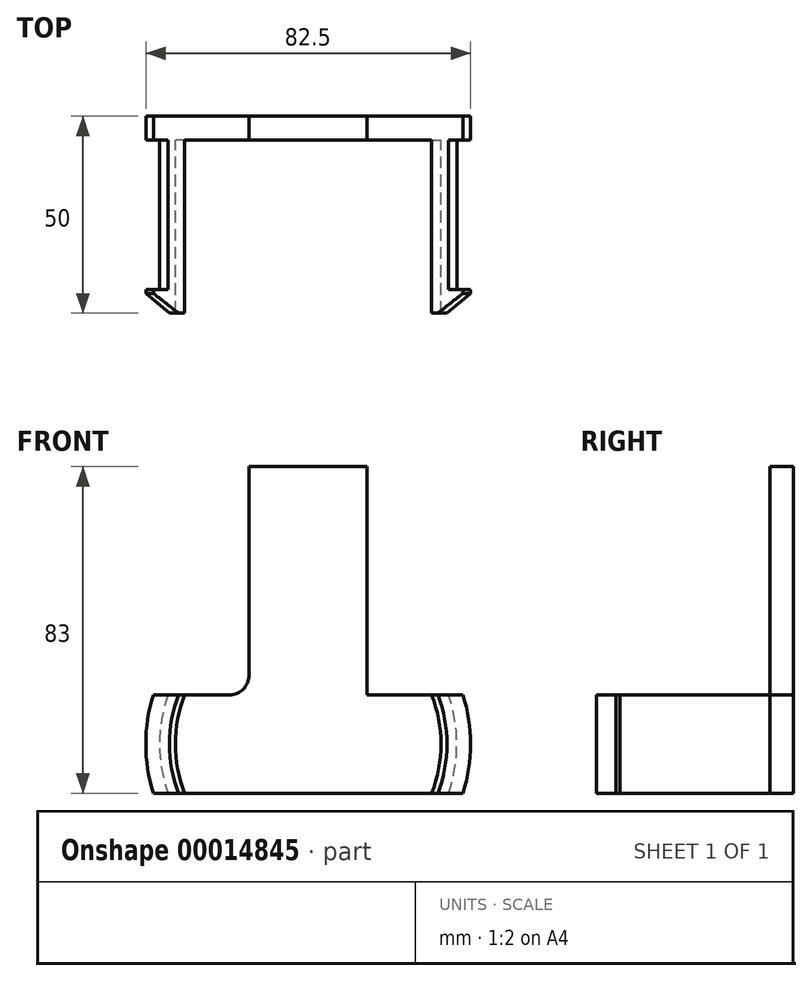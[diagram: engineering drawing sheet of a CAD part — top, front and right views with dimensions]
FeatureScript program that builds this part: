
annotation { "Feature Type Name" : "Feature", "Feature Type Description" : "" }
export const myFeature = defineFeature(function(context is Context, id is Id, definition is map)
    precondition{}
    {
        {
            var Q0;
            Q0=qCreatedBy(makeId("Front.planeOp"),FACE);
            var sketch = newSketch(context, id + "F0", { "sketchPlane" : qUnion([Q0])});
            skArc(sketch, "E0", {"start": v(-35.62, 12.5) * mm, "mid": v(-37.75, 0) * mm, "end": v(-35.62, -12.5) * mm});
            skLineSegment(sketch, "E1", {"start": v(-35.62, -12.5) * mm, "end": v(35.62, -12.5) * mm});
            skLineSegment(sketch, "E2", {"start": v(-35.62, 12.5) * mm, "end": v(35.62, 12.5) * mm});
            skLineSegment(sketch, "E3", {"start": v(-37.75, 0) * mm, "end": v(37.75, 0) * mm, "construction": true});
            skArc(sketch, "E4.trimOffspring", {"start": v(35.62, -12.5) * mm, "mid": v(37.75, 0) * mm, "end": v(35.62, 12.5) * mm});
            skArc(sketch, "E5.0", {"start": v(39.31, -12.5) * mm, "mid": v(41.25, 0) * mm, "end": v(39.31, 12.5) * mm});
            skArc(sketch, "E6.0", {"start": v(-39.31, 12.5) * mm, "mid": v(-41.25, 0) * mm, "end": v(-39.31, -12.5) * mm});
            skLineSegment(sketch, "E7", {"start": v(-35.62, 12.5) * mm, "end": v(-39.31, 12.5) * mm});
            skLineSegment(sketch, "E8", {"start": v(-35.62, -12.5) * mm, "end": v(-39.31, -12.5) * mm});
            skLineSegment(sketch, "E9", {"start": v(35.62, 12.5) * mm, "end": v(39.31, 12.5) * mm});
            skLineSegment(sketch, "E10", {"start": v(35.62, -12.5) * mm, "end": v(39.31, -12.5) * mm});
            skArc(sketch, "E11", {"start": v(-31.35, 12.5) * mm, "mid": v(-33.75, 0) * mm, "end": v(-31.35, -12.5) * mm});
            skArc(sketch, "E12.trimOffspring", {"start": v(31.35, -12.5) * mm, "mid": v(33.75, 0) * mm, "end": v(31.35, 12.5) * mm});
            skSolve(sketch);
        }
        {
            var Q0;
            {var subQ1=sQuery(id+"F0.wireOp",EDGE,"E11");Q0=makeQuery(id+"F0.imprint","IMPRINT",FACE,{"disambiguationData":[TD([[makeQuery(id+"F0.imprint","IMPRINT",EDGE,{"derivedFrom":subQ1}),1.0]])]});}
            extrude(context, id + "F1", {"entities" : qUnion([Q0]), "depth" : 6 * mm});
        }
        {
            var Q0;
            {var subQ2=sQuery(id+"F0.wireOp",EDGE,"E0");Q0=makeQuery(id+"F0.imprint","IMPRINT",FACE,{"disambiguationData":[TD([[makeQuery(id+"F0.imprint","IMPRINT",EDGE,{"derivedFrom":subQ2}),1.0]])]});}
            var Q1;
            {var subQ1=sQuery(id+"F0.wireOp",EDGE,"E4.trimOffspring");Q1=makeQuery(id+"F0.imprint","IMPRINT",FACE,{"disambiguationData":[TD([[makeQuery(id+"F0.imprint","IMPRINT",EDGE,{"derivedFrom":subQ1}),1.0]])]});}
            extrude(context, id + "F2", {"entities" : qUnion([Q0, Q1]), "operationType" : NewBodyOperationType.ADD, "depth" : 50 * mm});
        }
        {
            var Q0;
            Q0=makeQuery(id+"F0.imprint","IMPRINT",FACE,{"disambiguationData":[TD([[makeQuery(id+"F0.imprint","IMPRINT",EDGE,{"derivedFrom":sQuery(id+"F0.wireOp",EDGE,"E0")}),-1.0]])]});
            var Q1;
            Q1=makeQuery(id+"F0.imprint","IMPRINT",FACE,{"disambiguationData":[TD([[makeQuery(id+"F0.imprint","IMPRINT",EDGE,{"derivedFrom":sQuery(id+"F0.wireOp",EDGE,"E4.trimOffspring")}),-1.0]])]});
            extrude(context, id + "F3", {"entities" : qUnion([Q0, Q1]), "operationType" : NewBodyOperationType.ADD, "depth" : 50 * mm});
        }
        {
            var Q0;
            Q0=makeQuery(id+"F0.imprint","IMPRINT",FACE,{"disambiguationData":[TD([[makeQuery(id+"F0.imprint","IMPRINT",EDGE,{"derivedFrom":sQuery(id+"F0.wireOp",EDGE,"E0")}),-1.0]])]});
            var Q1;
            Q1=makeQuery(id+"F0.imprint","IMPRINT",FACE,{"disambiguationData":[TD([[makeQuery(id+"F0.imprint","IMPRINT",EDGE,{"derivedFrom":sQuery(id+"F0.wireOp",EDGE,"E4.trimOffspring")}),-1.0]])]});
            extrude(context, id + "F4", {"entities" : qUnion([Q0, Q1]), "operationType" : NewBodyOperationType.REMOVE, "depth" : 44 * mm});
        }
        {
            var Q0;
            Q0=makeQuery(id+"F0.imprint","IMPRINT",FACE,{"disambiguationData":[TD([[makeQuery(id+"F0.imprint","IMPRINT",EDGE,{"derivedFrom":sQuery(id+"F0.wireOp",EDGE,"E0")}),-1.0]])]});
            var Q1;
            Q1=makeQuery(id+"F0.imprint","IMPRINT",FACE,{"disambiguationData":[TD([[makeQuery(id+"F0.imprint","IMPRINT",EDGE,{"derivedFrom":sQuery(id+"F0.wireOp",EDGE,"E4.trimOffspring")}),-1.0]])]});
            extrude(context, id + "F5", {"entities" : qUnion([Q0, Q1]), "operationType" : NewBodyOperationType.ADD, "depth" : 6 * mm});
        }
        {
            var Q0;
            Q0=makeQuery(id+"F3.opExtrude","CAP_EDGE",EDGE,{"disambiguationData":[OSD([sQuery(id+"F0.wireOp",EDGE,"E5.0")])],"isStart":false});
            var Q1;
            Q1=makeQuery(id+"F3.opExtrude","CAP_EDGE",EDGE,{"disambiguationData":[OSD([sQuery(id+"F0.wireOp",EDGE,"E6.0")])],"isStart":false});
            chamfer(context, id + "F6", {"entities" : qUnion([Q0, Q1]), "chamferType" : ChamferType.TWO_OFFSETS, "width1" : 6 * mm, "oppositeDirection" : false, "width2" : 5 * mm, "tangentPropagation" : true});
        }
        {
            var Q0;
            {var subQ0=sQuery(id+"F0.wireOp",EDGE,"E2");var subQ1=sQuery(id+"F0.wireOp",EDGE,"E7");var subQ2=sQuery(id+"F0.wireOp",EDGE,"E9");Q0=makeQuery(id+"F5.boolean.opBoolean","MERGE",FACE,{"derivedFrom":[makeQuery(id+"F3.boolean.opBoolean","MERGE",FACE,{"derivedFrom":[makeQuery(id+"F2.boolean.opBoolean","MERGE",FACE,{"derivedFrom":[makeQuery(id+"F1.opExtrude","SWEPT_FACE",FACE,{"disambiguationData":[OSD([subQ0])]}),makeQuery(id+"F2.opExtrude","SWEPT_FACE",FACE,{"disambiguationData":[OSD([subQ0]),TDD([makeQuery(id+"F0.imprint","IMPRINT",EDGE,{"disambiguationData":[TD([[makeQuery(id+"F0.imprint","INTERSECT",VERTEX,{"derivedFrom":[subQ0,sQuery(id+"F0.wireOp",EDGE,"E11")]}),1.0]])],"derivedFrom":subQ0})])]}),makeQuery(id+"F2.opExtrude","SWEPT_FACE",FACE,{"disambiguationData":[OSD([subQ0]),TDD([makeQuery(id+"F0.imprint","IMPRINT",EDGE,{"disambiguationData":[TD([[makeQuery(id+"F0.imprint","INTERSECT",VERTEX,{"derivedFrom":[subQ0,sQuery(id+"F0.wireOp",EDGE,"E12.trimOffspring")]}),-1.0]])],"derivedFrom":subQ0})])]})]}),makeQuery(id+"F3.opExtrude","SWEPT_FACE",FACE,{"disambiguationData":[OSD([subQ1])]}),makeQuery(id+"F3.opExtrude","SWEPT_FACE",FACE,{"disambiguationData":[OSD([subQ2])]})]}),makeQuery(id+"F5.opExtrude","SWEPT_FACE",FACE,{"disambiguationData":[OSD([subQ1])]}),makeQuery(id+"F5.opExtrude","SWEPT_FACE",FACE,{"disambiguationData":[OSD([subQ2])]})]});}
            var sketch = newSketch(context, id + "F7", { "sketchPlane" : qUnion([Q0])});
            skLineSegment(sketch, "E13", {"start": v(15, -6) * mm, "end": v(15, 0) * mm});
            skLineSegment(sketch, "E14", {"start": v(-15, -6) * mm, "end": v(-15, 0) * mm});
            skLineSegment(sketch, "E15", {"start": v(0, -6) * mm, "end": v(0, 0) * mm, "construction": true});
            skSolve(sketch);
        }
        {
            var Q0;
            {var subQ5=sQuery(id+"F7.wireOp",EDGE,"E13");Q0=makeQuery(id+"F7.imprint","IMPRINT",FACE,{"disambiguationData":[TD([[makeQuery(id+"F7.imprint","IMPRINT",EDGE,{"derivedFrom":subQ5}),1.0]])]});}
            extrude(context, id + "F8", {"entities" : qUnion([Q0]), "operationType" : NewBodyOperationType.ADD, "depth" : 58 * mm});
        }
        {
            var Q0;
            Q0=makeQuery(id+"F8.opExtrude","CAP_EDGE",EDGE,{"disambiguationData":[OSD([sQuery(id+"F7.wireOp",EDGE,"E14")])],"isStart":true});
            var Q1;
            Q1=makeQuery(id+"F8.opExtrude","CAP_EDGE",EDGE,{"disambiguationData":[OSD([sQuery(id+"F7.wireOp",EDGE,"E13")])],"isStart":true});
            fillet(context, id + "F9", {"entities" : qUnion([Q0, Q1]), "radius" : 5 * mm, "tangentPropagation" : true, "allowEdgeOverflow" : false});
        }
    });
